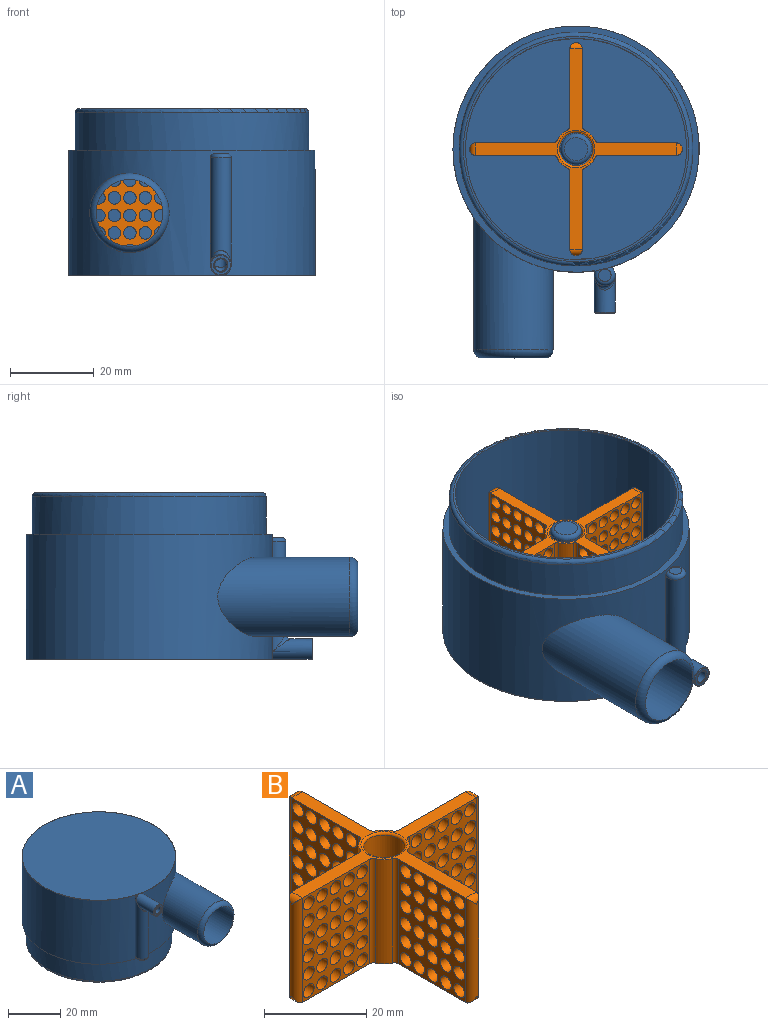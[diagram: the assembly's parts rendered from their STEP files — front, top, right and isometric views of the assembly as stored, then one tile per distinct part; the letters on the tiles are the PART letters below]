
ASSEMBLY  parts=2 mates=1
PART A: 41 faces, bbox 63.9x82.1x40.3 mm
  f0: cylinder r=26.5mm len=53mm, axis (0,0,1), area 5604.9mm2, adj f1,f34,f35,f40
  f1: bspline ~5x4.82mm, area 18.1mm2, adj f0,f2
  f2: cylinder r=1.5mm len=3.95mm, axis (0,1,0), area 26.4mm2, adj f1,f3,f4,f5
  f3: plane 0.85x0.06mm, normal (0,1,0), area 0mm2, adj f2,f5
  f4: plane 0.85x0.06mm, normal (0,1,0), area 0mm2, adj f2,f5
  f5: cylinder r=1.5mm len=26.2mm, axis (0,0,1), area 228.8mm2, adj f2,f3,f4,f6,f32,f33
  f6: bspline ~3x1.5mm, area 0mm2, adj f5,f7
  f7: cylinder r=1.5mm len=8.8mm, axis (0,-1,0), area 77mm2, adj f6,f8,f32
  f8: torus R=1.7mm, axis (0,-1,0), area 3.1mm2, adj f7,f9
  f9: plane 4.6x4.6mm, normal (0,-1,0), area 7.5mm2, adj f8,f10
  f10: torus R=2.3mm, axis (0,-1,0), area 4.8mm2, adj f9,f11
  f11: cylinder r=2.5mm len=10.3mm, axis (0,-1,0), area 128.1mm2, adj f10,f12,f21,f22,f30,f31
  f12: bspline ~2.95x2.5mm, area 2.4mm2, adj f11,f13,f17,f18,f22
  f13: cylinder r=29.5mm len=0.37mm, axis (0,0,1), area 0mm2, adj f12,f14
  f14: bspline ~0.56x0.19mm, area 0mm2, adj f13,f15,f16,f17,f22
  f15: torus R=29.44mm, axis (0,0,1), area 16.1mm2, adj f14,f16,f21,f22
  f16: plane 58.89x58.89mm, normal (0,0,1), area 2723.7mm2, adj f14,f15,f21
  f17: cylinder r=29.5mm len=0.2mm, axis (0,0,1), area 0mm2, adj f12,f14,f21
  f18: cylinder r=2.5mm len=26.88mm, axis (0,0,1), area 272.9mm2, adj f12,f19,f22,f30,f31
  f19: torus R=1.5mm, axis (0,0,-1), area 17.8mm2, adj f18,f20,f22
  f20: plane 3x3mm, normal (0,0,-1), area 7.1mm2, adj f19
  f21: bspline ~0.58x0.14mm, area 0mm2, adj f11,f15,f16,f17
  f22: cylinder r=29.5mm len=59mm, axis (0,0,1), area 5094.7mm2, adj f11,f12,f14,f15,f18,f19,f23,f27
  f23: cylinder r=9.5mm len=22.66mm, axis (0,-1,0), area 1352.7mm2, adj f22,f24
  f24: torus R=7.5mm, axis (0,-1,0), area 148.6mm2, adj f23,f25
  f25: cylinder r=8mm len=35.57mm, axis (0,1,0), area 1236.8mm2, adj f24,f26,f40
  f26: bspline ~10.65x10.4mm, area 58mm2, adj f25,f35,f40
  f27: plane 59x59mm, normal (0,0,-1), area 271mm2, adj f22,f28
  f28: cylinder r=28mm len=56mm, axis (0,0,1), area 1583.4mm2, adj f27,f29
  f29: torus R=27mm, axis (0,0,-1), area 272.8mm2, adj f28,f34
  f30: bspline ~2.12x2.12mm, area 0.9mm2, adj f11,f18,f22
  f31: bspline ~5x3.5mm, area 2.6mm2, adj f11,f18
  f32: bspline ~3x2.5mm, area 0mm2, adj f5,f7
  f33: plane 3x3mm, normal (0,0,1), area 7.1mm2, adj f5
  f34: plane 54x54mm, normal (0,0,-1), area 84mm2, adj f0,f29
  f35: plane 53.08x53.08mm, normal (0,0,-1), area 2167.7mm2, adj f0,f26,f36
  f36: cylinder r=3.5mm len=26mm, axis (0,0,1), area 571.8mm2, adj f35,f37
  f37: plane 7.5x7.5mm, normal (0,0,1), area 5.7mm2, adj f36,f38
  f38: torus R=2.75mm, axis (0,0,1), area 33.4mm2, adj f37,f39
  f39: plane 5.5x5.5mm, normal (0,0,-1), area 23.8mm2, adj f38
  f40: bspline ~25.52x21.88mm, area 377.6mm2, adj f0,f25,f26
PART B: 157 faces, bbox 51x51x25 mm
  f0: cylinder r=5mm len=25mm, axis (0,0,-1), area 88.9mm2, adj f5,f6,f150,f151
  f1: cylinder r=5mm len=25mm, axis (0,0,-1), area 88.9mm2, adj f5,f6,f152,f153
  f2: cylinder r=5mm len=25mm, axis (0,0,-1), area 88.9mm2, adj f5,f6,f154,f155
  f3: cylinder r=4mm len=24mm, axis (0,0,-1), area 603.2mm2, adj f147,f148
  f4: cylinder r=5mm len=25mm, axis (0,0,-1), area 88.9mm2, adj f5,f6,f149,f156
  f5: plane 48x48mm, normal (0,0,1), area 244.5mm2, adj f0,f1,f2,f4,f7,f8,f9,f42
  f6: plane 48x48mm, normal (0,0,-1), area 244.5mm2, adj f0,f1,f2,f4,f7,f8,f11,f42
  f7: plane 25x18.55mm, normal (0,-1,0), area 251.6mm2, adj f5,f6,f10,f12,f13,f14,f15,f16
  f8: plane 25x18.55mm, normal (0,1,0), area 251.6mm2, adj f5,f6,f10,f12,f13,f14,f15,f16
  f9: cylinder r=1.5mm len=3mm, axis (0,-1,0), area 4.5mm2, adj f5,f10
  f10: cylinder r=1.5mm len=25mm, axis (0,0,-1), area 112.7mm2, adj f7,f8,f9,f11
  f11: cylinder r=1.5mm len=3mm, axis (0,1,0), area 4.5mm2, adj f6,f10
  f12: cylinder r=1.5mm len=3mm, axis (0,-1,0), area 28.3mm2, adj f7,f8
  f13: cylinder r=1.5mm len=3mm, axis (0,-1,0), area 28.3mm2, adj f7,f8
  f14: cylinder r=1.5mm len=3mm, axis (0,-1,0), area 28.3mm2, adj f7,f8
  f15: cylinder r=1.5mm len=3mm, axis (0,-1,0), area 28.3mm2, adj f7,f8
  f16: cylinder r=1.5mm len=3mm, axis (0,-1,0), area 28.3mm2, adj f7,f8
  f17: cylinder r=1.5mm len=3mm, axis (0,-1,0), area 28.3mm2, adj f7,f8
  f18: cylinder r=1.5mm len=3mm, axis (0,-1,0), area 28.3mm2, adj f7,f8
  f19: cylinder r=1.5mm len=3mm, axis (0,-1,0), area 28.3mm2, adj f7,f8
  f20: cylinder r=1.5mm len=3mm, axis (0,-1,0), area 28.3mm2, adj f7,f8
  f21: cylinder r=1.5mm len=3mm, axis (0,-1,0), area 28.3mm2, adj f7,f8
  f22: cylinder r=1.5mm len=3mm, axis (0,-1,0), area 28.3mm2, adj f7,f8
  f23: cylinder r=1.5mm len=3mm, axis (0,-1,0), area 28.3mm2, adj f7,f8
  f24: cylinder r=1.5mm len=3mm, axis (0,-1,0), area 28.3mm2, adj f7,f8
  f25: cylinder r=1.5mm len=3mm, axis (0,-1,0), area 28.3mm2, adj f7,f8
  f26: cylinder r=1.5mm len=3mm, axis (0,-1,0), area 28.3mm2, adj f7,f8
  f27: cylinder r=1.5mm len=3mm, axis (0,-1,0), area 28.3mm2, adj f7,f8
  f28: cylinder r=1.5mm len=3mm, axis (0,-1,0), area 28.3mm2, adj f7,f8
  f29: cylinder r=1.5mm len=3mm, axis (0,-1,0), area 28.3mm2, adj f7,f8
  f30: cylinder r=1.5mm len=3mm, axis (0,-1,0), area 28.3mm2, adj f7,f8
  f31: cylinder r=1.5mm len=3mm, axis (0,-1,0), area 28.3mm2, adj f7,f8
  f32: cylinder r=1.5mm len=3mm, axis (0,-1,0), area 28.3mm2, adj f7,f8
  f33: cylinder r=1.5mm len=3mm, axis (0,-1,0), area 28.3mm2, adj f7,f8
  f34: cylinder r=1.5mm len=3mm, axis (0,-1,0), area 28.3mm2, adj f7,f8
  f35: cylinder r=1.5mm len=3mm, axis (0,-1,0), area 28.3mm2, adj f7,f8
  f36: cylinder r=1.5mm len=3mm, axis (0,-1,0), area 28.3mm2, adj f7,f8
  f37: cylinder r=1.5mm len=3mm, axis (0,-1,0), area 28.3mm2, adj f7,f8
  f38: cylinder r=1.5mm len=3mm, axis (0,-1,0), area 28.3mm2, adj f7,f8
  f39: cylinder r=1.5mm len=3mm, axis (0,-1,0), area 28.3mm2, adj f7,f8
  f40: cylinder r=1.5mm len=3mm, axis (0,-1,0), area 28.3mm2, adj f7,f8
  f41: cylinder r=1.5mm len=3mm, axis (0,-1,0), area 28.3mm2, adj f7,f8
  f42: plane 25x18.55mm, normal (-1,0,0), area 251.6mm2, adj f5,f6,f45,f47,f48,f49,f50,f51
  f43: plane 25x18.55mm, normal (1,0,0), area 251.6mm2, adj f5,f6,f45,f47,f48,f49,f50,f51
  f44: cylinder r=1.5mm len=3mm, axis (-1,0,0), area 4.5mm2, adj f5,f45
  f45: cylinder r=1.5mm len=25mm, axis (0,0,-1), area 112.7mm2, adj f42,f43,f44,f46
  f46: cylinder r=1.5mm len=3mm, axis (1,0,0), area 4.5mm2, adj f6,f45
  f47: cylinder r=1.5mm len=3mm, axis (-1,0,0), area 28.3mm2, adj f42,f43
  f48: cylinder r=1.5mm len=3mm, axis (-1,0,0), area 28.3mm2, adj f42,f43
  f49: cylinder r=1.5mm len=3mm, axis (-1,0,0), area 28.3mm2, adj f42,f43
  f50: cylinder r=1.5mm len=3mm, axis (-1,0,0), area 28.3mm2, adj f42,f43
  f51: cylinder r=1.5mm len=3mm, axis (-1,0,0), area 28.3mm2, adj f42,f43
  f52: cylinder r=1.5mm len=3mm, axis (-1,0,0), area 28.3mm2, adj f42,f43
  f53: cylinder r=1.5mm len=3mm, axis (-1,0,0), area 28.3mm2, adj f42,f43
  f54: cylinder r=1.5mm len=3mm, axis (-1,0,0), area 28.3mm2, adj f42,f43
  f55: cylinder r=1.5mm len=3mm, axis (-1,0,0), area 28.3mm2, adj f42,f43
  f56: cylinder r=1.5mm len=3mm, axis (-1,0,0), area 28.3mm2, adj f42,f43
  f57: cylinder r=1.5mm len=3mm, axis (-1,0,0), area 28.3mm2, adj f42,f43
  f58: cylinder r=1.5mm len=3mm, axis (-1,0,0), area 28.3mm2, adj f42,f43
  f59: cylinder r=1.5mm len=3mm, axis (-1,0,0), area 28.3mm2, adj f42,f43
  f60: cylinder r=1.5mm len=3mm, axis (-1,0,0), area 28.3mm2, adj f42,f43
  f61: cylinder r=1.5mm len=3mm, axis (-1,0,0), area 28.3mm2, adj f42,f43
  f62: cylinder r=1.5mm len=3mm, axis (-1,0,0), area 28.3mm2, adj f42,f43
  f63: cylinder r=1.5mm len=3mm, axis (-1,0,0), area 28.3mm2, adj f42,f43
  f64: cylinder r=1.5mm len=3mm, axis (-1,0,0), area 28.3mm2, adj f42,f43
  f65: cylinder r=1.5mm len=3mm, axis (-1,0,0), area 28.3mm2, adj f42,f43
  f66: cylinder r=1.5mm len=3mm, axis (-1,0,0), area 28.3mm2, adj f42,f43
  f67: cylinder r=1.5mm len=3mm, axis (-1,0,0), area 28.3mm2, adj f42,f43
  f68: cylinder r=1.5mm len=3mm, axis (-1,0,0), area 28.3mm2, adj f42,f43
  f69: cylinder r=1.5mm len=3mm, axis (-1,0,0), area 28.3mm2, adj f42,f43
  f70: cylinder r=1.5mm len=3mm, axis (-1,0,0), area 28.3mm2, adj f42,f43
  f71: cylinder r=1.5mm len=3mm, axis (-1,0,0), area 28.3mm2, adj f42,f43
  f72: cylinder r=1.5mm len=3mm, axis (-1,0,0), area 28.3mm2, adj f42,f43
  f73: cylinder r=1.5mm len=3mm, axis (-1,0,0), area 28.3mm2, adj f42,f43
  f74: cylinder r=1.5mm len=3mm, axis (-1,0,0), area 28.3mm2, adj f42,f43
  f75: cylinder r=1.5mm len=3mm, axis (-1,0,0), area 28.3mm2, adj f42,f43
  f76: cylinder r=1.5mm len=3mm, axis (-1,0,0), area 28.3mm2, adj f42,f43
  f77: plane 25x18.55mm, normal (0,1,0), area 251.6mm2, adj f5,f6,f80,f82,f83,f84,f85,f86
  f78: plane 25x18.55mm, normal (0,-1,0), area 251.6mm2, adj f5,f6,f80,f82,f83,f84,f85,f86
  f79: cylinder r=1.5mm len=3mm, axis (0,1,0), area 4.5mm2, adj f5,f80
  f80: cylinder r=1.5mm len=25mm, axis (0,0,-1), area 112.7mm2, adj f77,f78,f79,f81
  f81: cylinder r=1.5mm len=3mm, axis (0,-1,0), area 4.5mm2, adj f6,f80
  f82: cylinder r=1.5mm len=3mm, axis (0,1,0), area 28.3mm2, adj f77,f78
  f83: cylinder r=1.5mm len=3mm, axis (0,1,0), area 28.3mm2, adj f77,f78
  f84: cylinder r=1.5mm len=3mm, axis (0,1,0), area 28.3mm2, adj f77,f78
  f85: cylinder r=1.5mm len=3mm, axis (0,1,0), area 28.3mm2, adj f77,f78
  f86: cylinder r=1.5mm len=3mm, axis (0,1,0), area 28.3mm2, adj f77,f78
  f87: cylinder r=1.5mm len=3mm, axis (0,1,0), area 28.3mm2, adj f77,f78
  f88: cylinder r=1.5mm len=3mm, axis (0,1,0), area 28.3mm2, adj f77,f78
  f89: cylinder r=1.5mm len=3mm, axis (0,1,0), area 28.3mm2, adj f77,f78
  f90: cylinder r=1.5mm len=3mm, axis (0,1,0), area 28.3mm2, adj f77,f78
  f91: cylinder r=1.5mm len=3mm, axis (0,1,0), area 28.3mm2, adj f77,f78
  f92: cylinder r=1.5mm len=3mm, axis (0,1,0), area 28.3mm2, adj f77,f78
  f93: cylinder r=1.5mm len=3mm, axis (0,1,0), area 28.3mm2, adj f77,f78
  f94: cylinder r=1.5mm len=3mm, axis (0,1,0), area 28.3mm2, adj f77,f78
  f95: cylinder r=1.5mm len=3mm, axis (0,1,0), area 28.3mm2, adj f77,f78
  f96: cylinder r=1.5mm len=3mm, axis (0,1,0), area 28.3mm2, adj f77,f78
  f97: cylinder r=1.5mm len=3mm, axis (0,1,0), area 28.3mm2, adj f77,f78
  f98: cylinder r=1.5mm len=3mm, axis (0,1,0), area 28.3mm2, adj f77,f78
  f99: cylinder r=1.5mm len=3mm, axis (0,1,0), area 28.3mm2, adj f77,f78
  f100: cylinder r=1.5mm len=3mm, axis (0,1,0), area 28.3mm2, adj f77,f78
  f101: cylinder r=1.5mm len=3mm, axis (0,1,0), area 28.3mm2, adj f77,f78
  f102: cylinder r=1.5mm len=3mm, axis (0,1,0), area 28.3mm2, adj f77,f78
  f103: cylinder r=1.5mm len=3mm, axis (0,1,0), area 28.3mm2, adj f77,f78
  f104: cylinder r=1.5mm len=3mm, axis (0,1,0), area 28.3mm2, adj f77,f78
  f105: cylinder r=1.5mm len=3mm, axis (0,1,0), area 28.3mm2, adj f77,f78
  f106: cylinder r=1.5mm len=3mm, axis (0,1,0), area 28.3mm2, adj f77,f78
  f107: cylinder r=1.5mm len=3mm, axis (0,1,0), area 28.3mm2, adj f77,f78
  f108: cylinder r=1.5mm len=3mm, axis (0,1,0), area 28.3mm2, adj f77,f78
  f109: cylinder r=1.5mm len=3mm, axis (0,1,0), area 28.3mm2, adj f77,f78
  f110: cylinder r=1.5mm len=3mm, axis (0,1,0), area 28.3mm2, adj f77,f78
  f111: cylinder r=1.5mm len=3mm, axis (0,1,0), area 28.3mm2, adj f77,f78
  f112: plane 25x18.55mm, normal (1,0,0), area 251.6mm2, adj f5,f6,f115,f117,f118,f119,f120,f121
  f113: plane 25x18.55mm, normal (-1,0,0), area 251.6mm2, adj f5,f6,f115,f117,f118,f119,f120,f121
  f114: cylinder r=1.5mm len=3mm, axis (1,0,0), area 4.5mm2, adj f5,f115
  f115: cylinder r=1.5mm len=25mm, axis (0,0,-1), area 112.7mm2, adj f112,f113,f114,f116
  f116: cylinder r=1.5mm len=3mm, axis (-1,0,0), area 4.5mm2, adj f6,f115
  f117: cylinder r=1.5mm len=3mm, axis (1,0,0), area 28.3mm2, adj f112,f113
  f118: cylinder r=1.5mm len=3mm, axis (1,0,0), area 28.3mm2, adj f112,f113
  f119: cylinder r=1.5mm len=3mm, axis (1,0,0), area 28.3mm2, adj f112,f113
  f120: cylinder r=1.5mm len=3mm, axis (1,0,0), area 28.3mm2, adj f112,f113
  f121: cylinder r=1.5mm len=3mm, axis (1,0,0), area 28.3mm2, adj f112,f113
  f122: cylinder r=1.5mm len=3mm, axis (1,0,0), area 28.3mm2, adj f112,f113
  f123: cylinder r=1.5mm len=3mm, axis (1,0,0), area 28.3mm2, adj f112,f113
  f124: cylinder r=1.5mm len=3mm, axis (1,0,0), area 28.3mm2, adj f112,f113
  f125: cylinder r=1.5mm len=3mm, axis (1,0,0), area 28.3mm2, adj f112,f113
  f126: cylinder r=1.5mm len=3mm, axis (1,0,0), area 28.3mm2, adj f112,f113
  f127: cylinder r=1.5mm len=3mm, axis (1,0,0), area 28.3mm2, adj f112,f113
  f128: cylinder r=1.5mm len=3mm, axis (1,0,0), area 28.3mm2, adj f112,f113
  f129: cylinder r=1.5mm len=3mm, axis (1,0,0), area 28.3mm2, adj f112,f113
  f130: cylinder r=1.5mm len=3mm, axis (1,0,0), area 28.3mm2, adj f112,f113
  f131: cylinder r=1.5mm len=3mm, axis (1,0,0), area 28.3mm2, adj f112,f113
  f132: cylinder r=1.5mm len=3mm, axis (1,0,0), area 28.3mm2, adj f112,f113
  f133: cylinder r=1.5mm len=3mm, axis (1,0,0), area 28.3mm2, adj f112,f113
  f134: cylinder r=1.5mm len=3mm, axis (1,0,0), area 28.3mm2, adj f112,f113
  f135: cylinder r=1.5mm len=3mm, axis (1,0,0), area 28.3mm2, adj f112,f113
  f136: cylinder r=1.5mm len=3mm, axis (1,0,0), area 28.3mm2, adj f112,f113
  f137: cylinder r=1.5mm len=3mm, axis (1,0,0), area 28.3mm2, adj f112,f113
  f138: cylinder r=1.5mm len=3mm, axis (1,0,0), area 28.3mm2, adj f112,f113
  f139: cylinder r=1.5mm len=3mm, axis (1,0,0), area 28.3mm2, adj f112,f113
  f140: cylinder r=1.5mm len=3mm, axis (1,0,0), area 28.3mm2, adj f112,f113
  f141: cylinder r=1.5mm len=3mm, axis (1,0,0), area 28.3mm2, adj f112,f113
  f142: cylinder r=1.5mm len=3mm, axis (1,0,0), area 28.3mm2, adj f112,f113
  f143: cylinder r=1.5mm len=3mm, axis (1,0,0), area 28.3mm2, adj f112,f113
  f144: cylinder r=1.5mm len=3mm, axis (1,0,0), area 28.3mm2, adj f112,f113
  f145: cylinder r=1.5mm len=3mm, axis (1,0,0), area 28.3mm2, adj f112,f113
  f146: cylinder r=1.5mm len=3mm, axis (1,0,0), area 28.3mm2, adj f112,f113
  f147: torus R=4.5mm, axis (0,0,1), area 20.6mm2, adj f3,f6
  f148: torus R=4.5mm, axis (0,0,1), area 20.6mm2, adj f3,f5
  f149: cylinder r=1mm len=25mm, axis (0,0,-1), area 28.5mm2, adj f4,f5,f6,f112
  f150: cylinder r=1mm len=25mm, axis (0,0,-1), area 28.5mm2, adj f0,f5,f6,f113
  f151: cylinder r=1mm len=25mm, axis (0,0,-1), area 28.5mm2, adj f0,f5,f6,f77
  f152: cylinder r=1mm len=25mm, axis (0,0,-1), area 28.5mm2, adj f1,f5,f6,f78
  f153: cylinder r=1mm len=25mm, axis (0,0,-1), area 28.5mm2, adj f1,f5,f6,f42
  f154: cylinder r=1mm len=25mm, axis (0,0,-1), area 28.5mm2, adj f2,f5,f6,f43
  f155: cylinder r=1mm len=25mm, axis (0,0,-1), area 28.5mm2, adj f2,f5,f6,f7
  f156: cylinder r=1mm len=25mm, axis (0,0,-1), area 28.5mm2, adj f4,f5,f6,f8
PLACE A rot(axis=(0,-1,0),180deg) t=(0.18,-5.51,-0.84)mm
PLACE B rot(axis=(0,0,-1),180deg) t=(0.18,-5.51,3.16)mm
MATE revolute B.f0 <-> A.f28  axis (0,0,1) through (0.18,-5.51,28.16)mm
